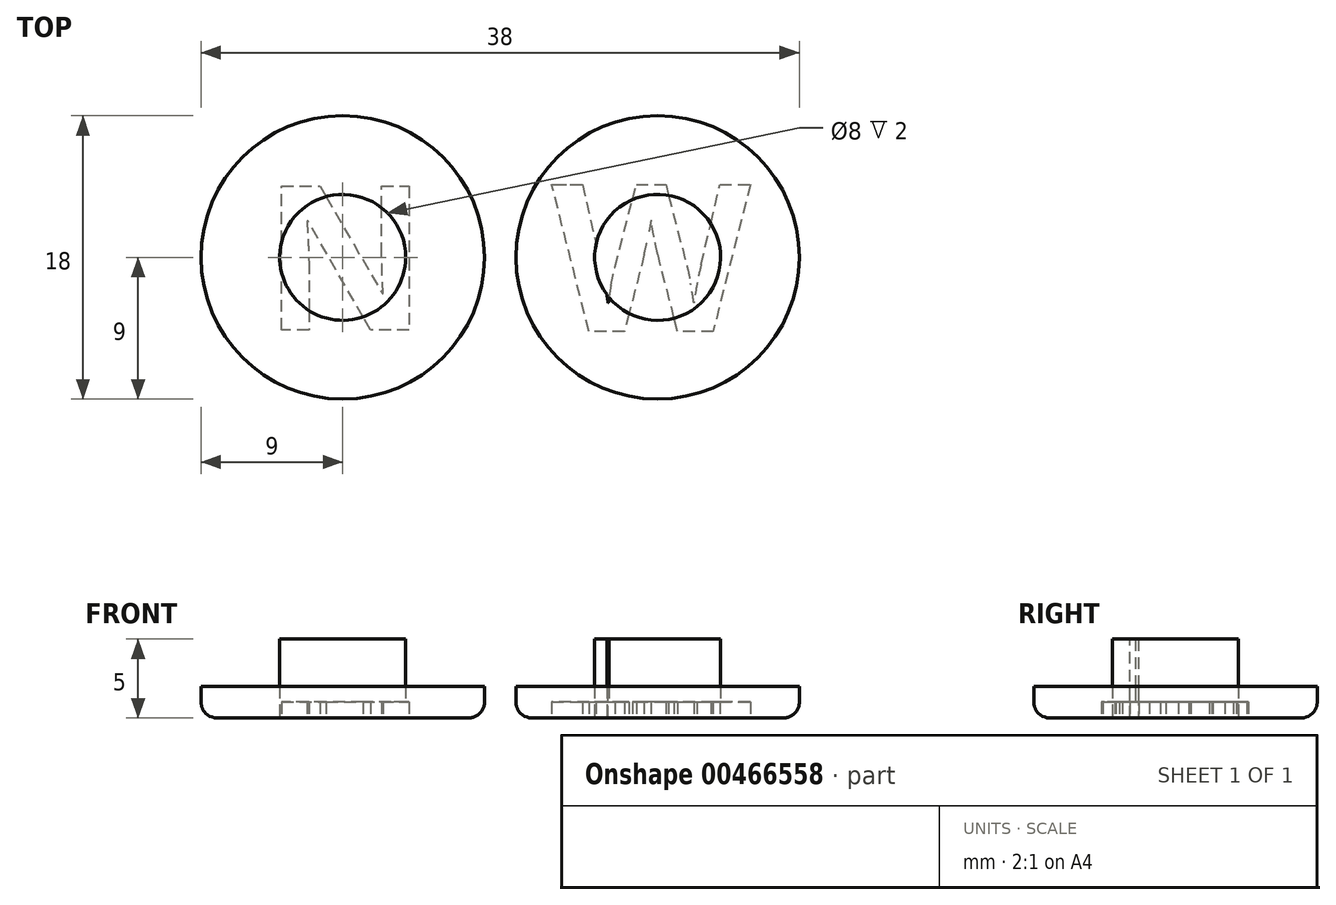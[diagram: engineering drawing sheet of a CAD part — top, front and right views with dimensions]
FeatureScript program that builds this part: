
annotation { "Feature Type Name" : "Feature", "Feature Type Description" : "" }
export const myFeature = defineFeature(function(context is Context, id is Id, definition is map)
    precondition{}
    {
        {
            var Q0;
            Q0=qCreatedBy(makeId("Top.planeOp"),FACE);
            var sketch = newSketch(context, id + "F0", { "sketchPlane" : qUnion([Q0])});
            skCircle(sketch, "E0", {"center": v(0, 0) * mm, "radius": 9 * mm});
            skCircle(sketch, "E1", {"center": v(0, 0) * mm, "radius": 4 * mm});
            skPoint(sketch, "E2", {"position": v(5.03, 4.6) * mm});
            skPoint(sketch, "E3.1.0", {"position": v(-4.6, 5.03) * mm});
            skPoint(sketch, "E3.2.0", {"position": v(-5.03, -4.6) * mm});
            skPoint(sketch, "E3.3.0", {"position": v(4.6, -5.03) * mm});
            skText(sketch, "E4", { "text": "N", "fontName": "OpenSans-Bold.ttf"});
            skCircle(sketch, "E5.1.0.0", {"center": v(20, 0) * mm, "radius": 9 * mm});
            skCircle(sketch, "E5.1.0.1", {"center": v(20, 0) * mm, "radius": 4 * mm});
            skLineSegment(sketch, "E5.direction1", {"start": v(0, 0) * mm, "end": v(20, 0) * mm, "construction": true});
            skPoint(sketch, "E6", {"position": v(26.73, 4.7) * mm});
            skPoint(sketch, "E7.1.0", {"position": v(15.3, 6.73) * mm});
            skPoint(sketch, "E7.2.0", {"position": v(13.27, -4.7) * mm});
            skPoint(sketch, "E7.3.0", {"position": v(24.7, -6.73) * mm});
            skText(sketch, "E8", { "text": "W", "fontName": "OpenSans-Bold.ttf"});
            const initialGuessF0  = {"E4": [-0.00503, -0.0046, 1, 0, 0.0092], "E8": [0.01327, -0.0047, 1, 0, 0.0094]};
            skSetInitialGuess(sketch, initialGuessF0);
            skSolve(sketch);
        }
        {
            var Q0;
            Q0=makeQuery(id+"F0.imprint","IMPRINT",FACE,{"disambiguationData":[TD([[makeQuery(id+"F0.imprint","IMPRINT",EDGE,{"derivedFrom":sQuery(id+"F0.wireOp",EDGE,"E0")}),1.0]])]});
            var Q1;
            Q1=makeQuery(id+"F0.imprint","IMPRINT",FACE,{"disambiguationData":[TD([[makeQuery(id+"F0.imprint","IMPRINT",EDGE,{"derivedFrom":sQuery(id+"F0.wireOp",EDGE,"E5.1.0.0")}),1.0]])]});
            var Q2;
            {var subQ5=sQuery(id+"F0.wireOp",EDGE,"E4.sketch_text.stroke-7");Q2=makeQuery(id+"F0.imprint","IMPRINT",FACE,{"disambiguationData":[TD([[makeQuery(id+"F0.imprint","IMPRINT",EDGE,{"derivedFrom":subQ5}),-1.0]])]});}
            var Q3;
            {var subQ5=sQuery(id+"F0.wireOp",EDGE,"E4.sketch_text.stroke-5");Q3=makeQuery(id+"F0.imprint","IMPRINT",FACE,{"disambiguationData":[TD([[makeQuery(id+"F0.imprint","IMPRINT",EDGE,{"derivedFrom":subQ5}),-1.0]])]});}
            var Q4;
            {var subQ5=sQuery(id+"F0.wireOp",EDGE,"E4.sketch_text.stroke-0");Q4=makeQuery(id+"F0.imprint","IMPRINT",FACE,{"disambiguationData":[TD([[makeQuery(id+"F0.imprint","IMPRINT",EDGE,{"derivedFrom":subQ5}),-1.0]])]});}
            var Q5;
            {var subQ0=sQuery(id+"F0.wireOp",EDGE,"E8.sketch_text.stroke-7");Q5=makeQuery(id+"F0.imprint","IMPRINT",FACE,{"disambiguationData":[TD([[makeQuery(id+"F0.imprint","IMPRINT",EDGE,{"derivedFrom":subQ0}),-1.0]])]});}
            var Q6;
            {var subQ5=sQuery(id+"F0.wireOp",EDGE,"E8.sketch_text.stroke-15");Q6=makeQuery(id+"F0.imprint","IMPRINT",FACE,{"disambiguationData":[TD([[makeQuery(id+"F0.imprint","IMPRINT",EDGE,{"derivedFrom":subQ5}),-1.0]])]});}
            var Q7;
            {var subQ1=sQuery(id+"F0.wireOp",EDGE,"E8.sketch_text.stroke-0");Q7=makeQuery(id+"F0.imprint","IMPRINT",FACE,{"disambiguationData":[TD([[makeQuery(id+"F0.imprint","IMPRINT",EDGE,{"derivedFrom":subQ1}),-1.0]])]});}
            extrude(context, id + "F1", {"entities" : qUnion([Q0, Q1, Q2, Q3, Q4, Q5, Q6, Q7]), "depth" : 2 * mm});
        }
        {
            var Q0;
            {var subQ0=sQuery(id+"F0.wireOp",EDGE,"E8.sketch_text.stroke-2");Q0=makeQuery(id+"F0.imprint","IMPRINT",FACE,{"disambiguationData":[TD([[makeQuery(id+"F0.imprint","IMPRINT",EDGE,{"derivedFrom":subQ0}),1.0]])]});}
            var Q1;
            {var subQ10=sQuery(id+"F0.wireOp",EDGE,"E8.sketch_text.stroke-2");Q1=makeQuery(id+"F0.imprint","IMPRINT",FACE,{"disambiguationData":[TD([[makeQuery(id+"F0.imprint","IMPRINT",EDGE,{"derivedFrom":subQ10}),-1.0]])]});}
            var Q2;
            {var subQ5=sQuery(id+"F0.wireOp",EDGE,"E8.sketch_text.stroke-17");Q2=makeQuery(id+"F0.imprint","IMPRINT",FACE,{"disambiguationData":[TD([[makeQuery(id+"F0.imprint","IMPRINT",EDGE,{"derivedFrom":subQ5}),1.0]])]});}
            var Q3;
            {var subQ0=sQuery(id+"F0.wireOp",EDGE,"E8.sketch_text.stroke-11");var subQ1=sQuery(id+"F0.wireOp",EDGE,"E5.1.0.1");var subQ2=makeQuery(id+"F0.imprint","INTERSECT",VERTEX,{"derivedFrom":[subQ1,subQ0]});Q3=makeQuery(id+"F0.imprint","IMPRINT",FACE,{"disambiguationData":[TD([[makeQuery(id+"F0.imprint","IMPRINT",EDGE,{"disambiguationData":[TD([[subQ2,-1.0]])],"derivedFrom":subQ1}),-1.0]])]});}
            var Q4;
            {var subQ8=sQuery(id+"F0.wireOp",EDGE,"E8.sketch_text.stroke-13");Q4=makeQuery(id+"F0.imprint","IMPRINT",FACE,{"disambiguationData":[TD([[makeQuery(id+"F0.imprint","IMPRINT",EDGE,{"derivedFrom":subQ8}),1.0]])]});}
            var Q5;
            {var subQ0=sQuery(id+"F0.wireOp",EDGE,"E8.sketch_text.stroke-10");var subQ1=sQuery(id+"F0.wireOp",EDGE,"E5.1.0.1");var subQ2=makeQuery(id+"F0.imprint","INTERSECT",VERTEX,{"derivedFrom":[subQ1,subQ0]});Q5=makeQuery(id+"F0.imprint","IMPRINT",FACE,{"disambiguationData":[TD([[makeQuery(id+"F0.imprint","IMPRINT",EDGE,{"disambiguationData":[TD([[subQ2,-1.0]])],"derivedFrom":subQ1}),1.0]])]});}
            var Q6;
            {var subQ1=sQuery(id+"F0.wireOp",EDGE,"E4.sketch_text.stroke-9");Q6=makeQuery(id+"F0.imprint","IMPRINT",FACE,{"disambiguationData":[TD([[makeQuery(id+"F0.imprint","IMPRINT",EDGE,{"derivedFrom":subQ1}),1.0]])]});}
            var Q7;
            {var subQ1=sQuery(id+"F0.wireOp",EDGE,"E4.sketch_text.stroke-2");Q7=makeQuery(id+"F0.imprint","IMPRINT",FACE,{"disambiguationData":[TD([[makeQuery(id+"F0.imprint","IMPRINT",EDGE,{"derivedFrom":subQ1}),1.0]])]});}
            var Q8;
            {var subQ8=sQuery(id+"F0.wireOp",EDGE,"E4.sketch_text.stroke-2");Q8=makeQuery(id+"F0.imprint","IMPRINT",FACE,{"disambiguationData":[TD([[makeQuery(id+"F0.imprint","IMPRINT",EDGE,{"derivedFrom":subQ8}),-1.0]])]});}
            var Q9;
            {var subQ0=sQuery(id+"F0.wireOp",EDGE,"E4.sketch_text.stroke-6");var subQ1=sQuery(id+"F0.wireOp",EDGE,"E1");var subQ2=makeQuery(id+"F0.imprint","INTERSECT",VERTEX,{"disambiguationData":[OD(0.0)],"derivedFrom":[subQ1,subQ0]});Q9=makeQuery(id+"F0.imprint","IMPRINT",FACE,{"disambiguationData":[TD([[makeQuery(id+"F0.imprint","IMPRINT",EDGE,{"disambiguationData":[TD([[subQ2,-1.0]])],"derivedFrom":subQ1}),1.0]])]});}
            extrude(context, id + "F2", {"entities" : qUnion([Q0, Q1, Q2, Q3, Q4, Q5, Q6, Q7, Q8, Q9]), "depth" : 5 * mm});
        }
        {
            var Q0;
            {var subQ5=sQuery(id+"F0.wireOp",EDGE,"E8.sketch_text.stroke-15");Q0=makeQuery(id+"F0.imprint","IMPRINT",FACE,{"disambiguationData":[TD([[makeQuery(id+"F0.imprint","IMPRINT",EDGE,{"derivedFrom":subQ5}),-1.0]])]});}
            var Q1;
            {var subQ1=sQuery(id+"F0.wireOp",EDGE,"E8.sketch_text.stroke-0");Q1=makeQuery(id+"F0.imprint","IMPRINT",FACE,{"disambiguationData":[TD([[makeQuery(id+"F0.imprint","IMPRINT",EDGE,{"derivedFrom":subQ1}),-1.0]])]});}
            var Q2;
            {var subQ10=sQuery(id+"F0.wireOp",EDGE,"E8.sketch_text.stroke-2");Q2=makeQuery(id+"F0.imprint","IMPRINT",FACE,{"disambiguationData":[TD([[makeQuery(id+"F0.imprint","IMPRINT",EDGE,{"derivedFrom":subQ10}),-1.0]])]});}
            var Q3;
            {var subQ0=sQuery(id+"F0.wireOp",EDGE,"E8.sketch_text.stroke-7");Q3=makeQuery(id+"F0.imprint","IMPRINT",FACE,{"disambiguationData":[TD([[makeQuery(id+"F0.imprint","IMPRINT",EDGE,{"derivedFrom":subQ0}),-1.0]])]});}
            var Q4;
            {var subQ5=sQuery(id+"F0.wireOp",EDGE,"E4.sketch_text.stroke-0");Q4=makeQuery(id+"F0.imprint","IMPRINT",FACE,{"disambiguationData":[TD([[makeQuery(id+"F0.imprint","IMPRINT",EDGE,{"derivedFrom":subQ5}),-1.0]])]});}
            var Q5;
            {var subQ8=sQuery(id+"F0.wireOp",EDGE,"E4.sketch_text.stroke-2");Q5=makeQuery(id+"F0.imprint","IMPRINT",FACE,{"disambiguationData":[TD([[makeQuery(id+"F0.imprint","IMPRINT",EDGE,{"derivedFrom":subQ8}),-1.0]])]});}
            var Q6;
            {var subQ5=sQuery(id+"F0.wireOp",EDGE,"E4.sketch_text.stroke-5");Q6=makeQuery(id+"F0.imprint","IMPRINT",FACE,{"disambiguationData":[TD([[makeQuery(id+"F0.imprint","IMPRINT",EDGE,{"derivedFrom":subQ5}),-1.0]])]});}
            var Q7;
            {var subQ5=sQuery(id+"F0.wireOp",EDGE,"E4.sketch_text.stroke-7");Q7=makeQuery(id+"F0.imprint","IMPRINT",FACE,{"disambiguationData":[TD([[makeQuery(id+"F0.imprint","IMPRINT",EDGE,{"derivedFrom":subQ5}),-1.0]])]});}
            extrude(context, id + "F3", {"entities" : qUnion([Q0, Q1, Q2, Q3, Q4, Q5, Q6, Q7]), "operationType" : NewBodyOperationType.REMOVE, "depth" : 1 * mm});
        }
        {
            var Q0;
            Q0=makeQuery(id+"F1.opExtrude","CAP_EDGE",EDGE,{"disambiguationData":[OSD([sQuery(id+"F0.wireOp",EDGE,"E0")])],"isStart":true});
            var Q1;
            Q1=makeQuery(id+"F1.opExtrude","CAP_EDGE",EDGE,{"disambiguationData":[OSD([sQuery(id+"F0.wireOp",EDGE,"E5.1.0.0")])],"isStart":true});
            fillet(context, id + "F4", {"entities" : qUnion([Q0, Q1]), "radius" : 1 * mm, "tangentPropagation" : true, "allowEdgeOverflow" : false});
        }
    });
